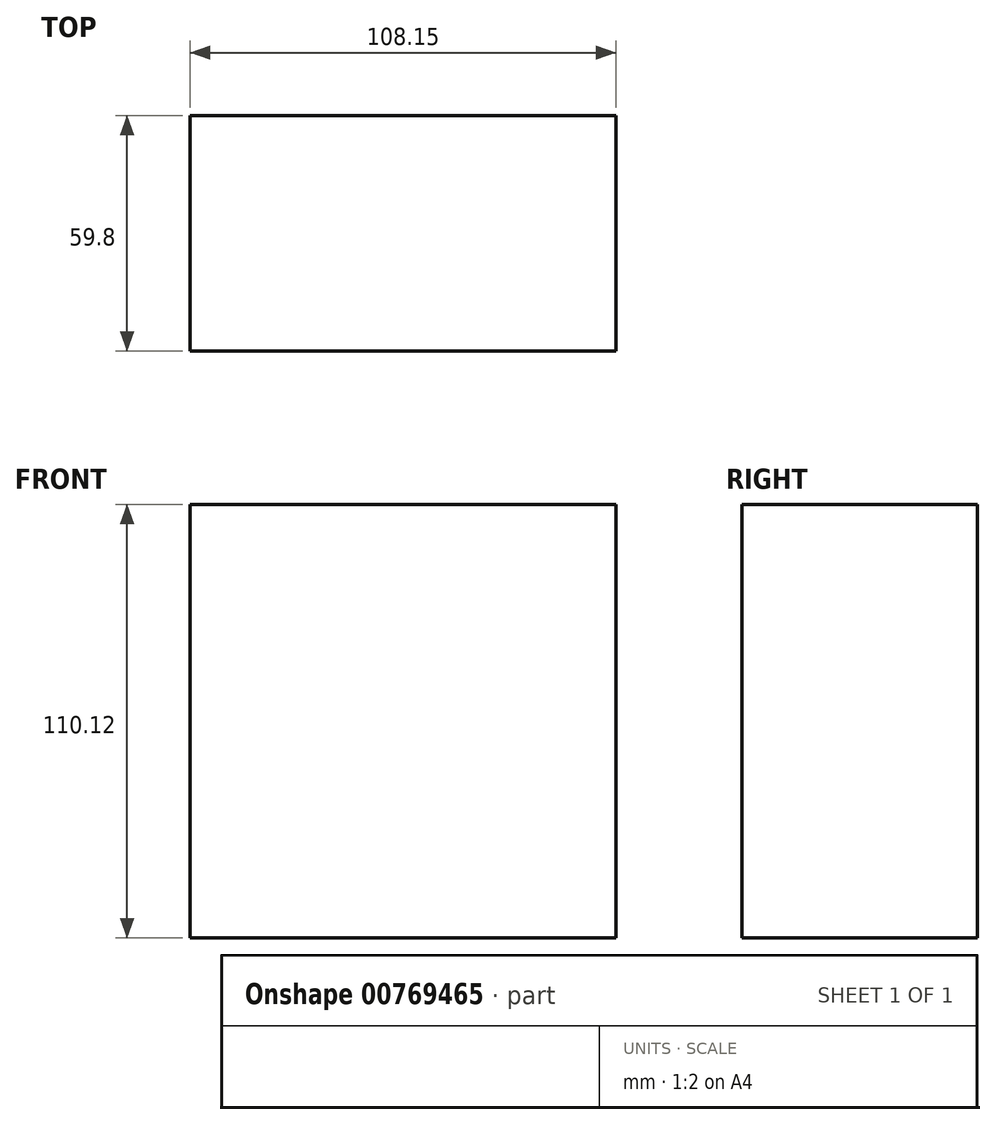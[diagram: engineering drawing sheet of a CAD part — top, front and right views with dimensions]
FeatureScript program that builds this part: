
annotation { "Feature Type Name" : "Feature", "Feature Type Description" : "" }
export const myFeature = defineFeature(function(context is Context, id is Id, definition is map)
    precondition{}
    {
        {
            var Q0;
            Q0=qCreatedBy(makeId("Front.planeOp"),FACE);
            var sketch = newSketch(context, id + "F0", { "sketchPlane" : qUnion([Q0])});
            skLineSegment(sketch, "E0.bottom", {"start": v(-36.66, 40.9) * mm, "end": v(71.5, 40.9) * mm});
            skLineSegment(sketch, "E0.top", {"start": v(-36.66, -69.23) * mm, "end": v(71.5, -69.23) * mm});
            skLineSegment(sketch, "E0.left", {"start": v(-36.66, 40.9) * mm, "end": v(-36.66, -69.23) * mm});
            skLineSegment(sketch, "E0.right", {"start": v(71.5, 40.9) * mm, "end": v(71.5, -69.23) * mm});
            skSolve(sketch);
        }
        {
            var Q0;
            Q0=makeQuery(id+"F0.imprint","IMPRINT",FACE,{"disambiguationData":[TD([[makeQuery(id+"F0.imprint","IMPRINT",EDGE,{"derivedFrom":sQuery(id+"F0.wireOp",EDGE,"E0.bottom")}),-1.0]])]});
            extrude(context, id + "F1", {"entities" : qUnion([Q0]), "depth" : 59.8 * mm, "offsetDistance" : 25.4 * mm});
        }
    });
